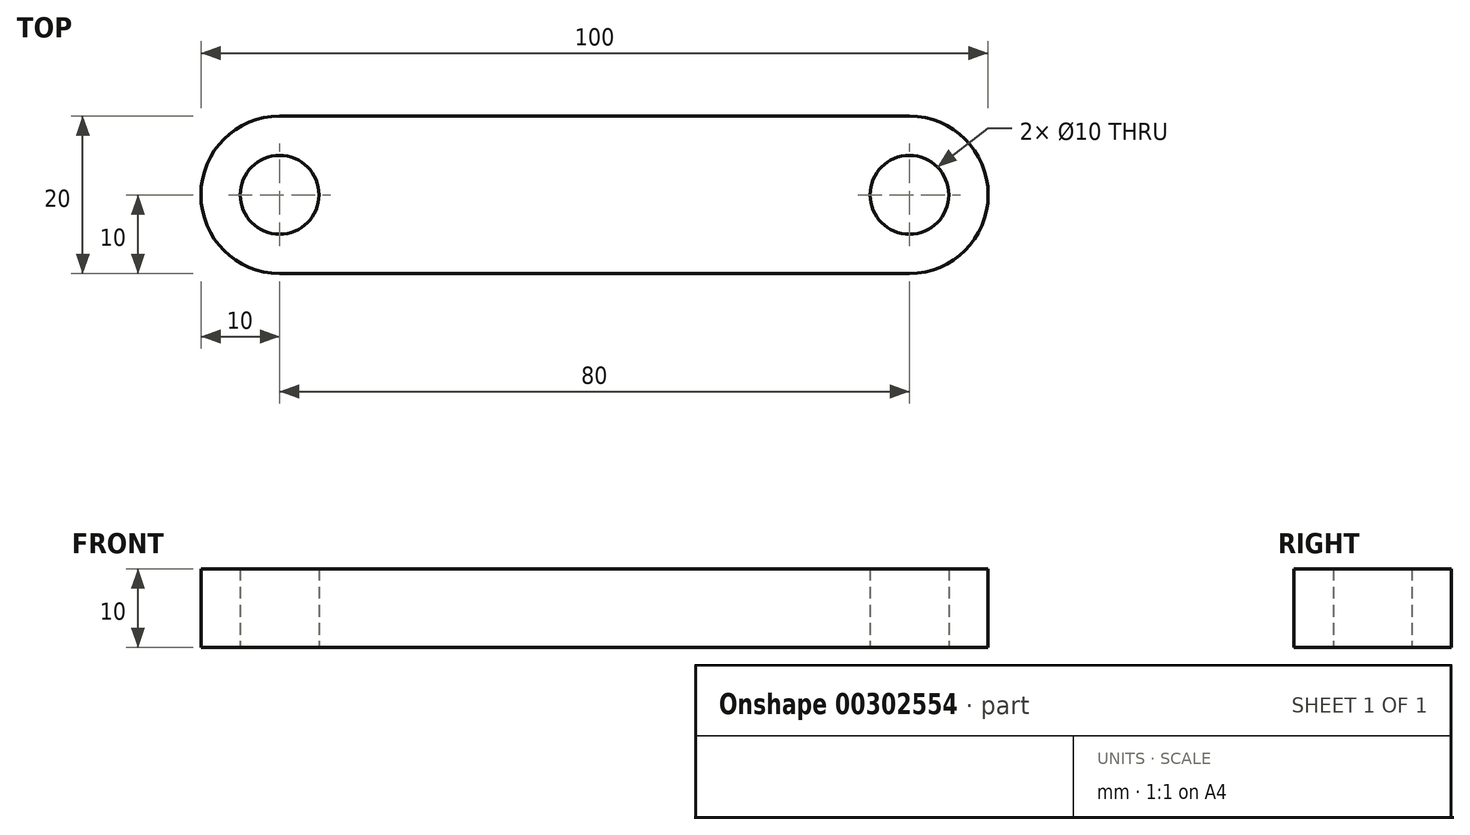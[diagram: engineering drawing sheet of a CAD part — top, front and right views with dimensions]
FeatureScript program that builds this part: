
annotation { "Feature Type Name" : "Feature", "Feature Type Description" : "" }
export const myFeature = defineFeature(function(context is Context, id is Id, definition is map)
    precondition{}
    {
        {
            var Q0;
            Q0=qCreatedBy(makeId("Top.planeOp"),FACE);
            var sketch = newSketch(context, id + "F0", { "sketchPlane" : qUnion([Q0])});
            skLineSegment(sketch, "E0", {"start": v(-80, 0) * mm, "end": v(0, 0) * mm, "construction": true});
            skArc(sketch, "E1.0.startCap", {"start": v(-80, -10) * mm, "mid": v(-90, 0) * mm, "end": v(-80, 10) * mm});
            skArc(sketch, "E1.0.endCap", {"start": v(0, 10) * mm, "mid": v(10, 0) * mm, "end": v(0, -10) * mm});
            skLineSegment(sketch, "E1.0.left", {"start": v(-80, 10) * mm, "end": v(0, 10) * mm});
            skLineSegment(sketch, "E1.0.right", {"start": v(-80, -10) * mm, "end": v(0, -10) * mm});
            skCircle(sketch, "E2", {"center": v(-80, 0) * mm, "radius": 5 * mm});
            skCircle(sketch, "E3", {"center": v(0, 0) * mm, "radius": 5 * mm});
            skSolve(sketch);
        }
        {
            var Q0;
            Q0 = qSketchRegion(id + "F0", true);
            extrude(context, id + "F1", {"entities" : qUnion([Q0]), "depth" : 10 * mm});
        }
    });
